# Revit family: 53-40-005-DN32-80
name_source: partatom
category: Pipe Accessories
units: mm (PartAtom-declared; Revit-internal decimal feet)

## family parameters
Always vertical = Yes
Cut with Voids When Loaded = No
Part Type = Valve - Breaks Into
Round Connector Dimension = Use Diameter
Shared = No
Work Plane-Based = No

## types (5) — shared parameters
Body_Wall_thickness = 10 mm  [stored 0.0328084 ft]
Circle_cut = 2 mm  [stored 0.00656168 ft]
DN = 50 mm
DN32_PN10 = 53-032-40-9090
DN40_PN10 = 53-040-40-9090
DN50_PN10 = 53-050-40-9090
DN65_PN10 = 53-065-40-9090
DN80_PN10 = 53-080-40-9090
Description_ = AVK BALL CHECK VALVE, THREADED
Ear_Height = 5 mm  [stored 0.0164042 ft]
Ear_width = 5 mm  [stored 0.0164042 ft]
Hook_Distance = 10 mm  [stored 0.0328084 ft]
RF_Thickness = 3 mm  [stored 0.00984252 ft]
Search_table = 53-40-005-DN32-80
URL product pages = https://www.avkvalves.com

## per-type parameters (varying)
- DN050: Body_Height_1=33 mm  [stored 0.108268 ft]; Body_Height_2=77 mm; Body_Height_3=37 mm  [stored 0.121391 ft]; Body_Ref=71 mm; Body_distance_1=10 mm  [stored 0.0328084 ft]; Body_distance_3=20 mm  [stored 0.0656168 ft]; Bottom_height=5 mm  [stored 0.0164042 ft]; Chamfer=20 mm  [stored 0.0656168 ft]; Chamfer_Ref=46 mm  [stored 0.150919 ft]; Circle_Height=20 mm  [stored 0.0656168 ft]; Circle_Height_2=10 mm  [stored 0.0328084 ft]; Circle_Length=35 mm  [stored 0.114829 ft]; Circle_Radius_2=475 mm; Circle_radius=40 mm  [stored 0.131234 ft]; Cut_Height_Ref=67.33 mm; Cut_ref=35 mm  [stored 0.114829 ft]; DN_ref=70 mm; Distance_1=5 mm  [stored 0.0164042 ft]; Distance_2=51 mm; Distance_3=67 mm; Distance_4=2 mm  [stored 0.00656168 ft]; Ear_Lenght_2=31 mm  [stored 0.101706 ft]; Ear_Length=62 mm; Ear_Reference=73 mm; Ear_Reference_2=3 mm  [stored 0.00984252 ft]; F_OD=82.5 mm; Fillet_Thickness_2=3 mm  [stored 0.00984252 ft]; Flange_Dia=43 mm  [stored 0.141076 ft]; Flange_Thickness=19 mm  [stored 0.062336 ft]; Flange_Thickness_2=5 mm  [stored 0.0164042 ft]; H=101 mm; H3=144 mm; H3_ref=43 mm  [stored 0.141076 ft]; Hook_Distance_2=2 mm  [stored 0.00656168 ft]; Hook_Height=10 mm  [stored 0.0328084 ft]; Hook_Height_2=5 mm  [stored 0.0164042 ft]; Hook_Legnth=5 mm  [stored 0.0164042 ft]; ID=25 mm  [stored 0.082021 ft]; L=180 mm; L2=270 mm; Nominal_Diameter=50 mm; RF=49 mm  [stored 0.160761 ft]; Rib_Distance=10 mm  [stored 0.0328084 ft]; Rib_Distance_2=10 mm  [stored 0.0328084 ft]; Rib_height=20 mm  [stored 0.0656168 ft]
- DN032: Body_Height_1=26 mm; Body_Height_2=55 mm; Body_Height_3=29 mm  [stored 0.0951444 ft]; Body_Ref=51 mm; Body_distance_1=8 mm  [stored 0.0262467 ft]; Body_distance_3=15 mm  [stored 0.0492126 ft]; Bottom_height=3 mm  [stored 0.00984252 ft]; Chamfer=15 mm  [stored 0.0492126 ft]; Chamfer_Ref=35.5 mm  [stored 0.11647 ft]; Circle_Height=12 mm  [stored 0.0393701 ft]; Circle_Height_2=8 mm  [stored 0.0262467 ft]; Circle_Length=25 mm  [stored 0.082021 ft]; Circle_Radius_2=320 mm; Circle_radius=30 mm  [stored 0.0984252 ft]; Cut_Height_Ref=55.33 mm; Cut_ref=26 mm; DN_ref=52 mm; Distance_1=2 mm  [stored 0.00656168 ft]; Distance_2=40 mm  [stored 0.131234 ft]; Distance_3=55 mm; Distance_4=10 mm  [stored 0.0328084 ft]; Ear_Lenght_2=26.75 mm  [stored 0.0877625 ft]; Ear_Length=53.5 mm; Ear_Reference=65 mm; Ear_Reference_2=3 mm  [stored 0.00984252 ft]; F_OD=77.5 mm; Fillet_Thickness_2=3 mm  [stored 0.00984252 ft]; Flange_Dia=31 mm  [stored 0.101706 ft]; Flange_Thickness=19 mm  [stored 0.062336 ft]; Flange_Thickness_2=4 mm  [stored 0.0131234 ft]; H=83 mm; H3=118 mm; H3_ref=35 mm  [stored 0.114829 ft]; Hook_Distance_2=2 mm  [stored 0.00656168 ft]; Hook_Height=10 mm  [stored 0.0328084 ft]; Hook_Height_2=5 mm  [stored 0.0164042 ft]; Hook_Legnth=5 mm  [stored 0.0164042 ft]; ID=16 mm  [stored 0.0524934 ft]; L=140 mm; L2=210 mm; Nominal_Diameter=32 mm  [stored 0.104987 ft]; RF=44 mm  [stored 0.144357 ft]; Rib_Distance=10 mm  [stored 0.0328084 ft]; Rib_Distance_2=10 mm  [stored 0.0328084 ft]; Rib_height=15 mm  [stored 0.0492126 ft]
- DN040: Body_Height_1=30 mm  [stored 0.0984252 ft]; Body_Height_2=55 mm; Body_Height_3=30 mm  [stored 0.0984252 ft]; Body_Ref=51 mm; Body_distance_1=8 mm  [stored 0.0262467 ft]; Body_distance_3=15 mm  [stored 0.0492126 ft]; Bottom_height=3 mm  [stored 0.00984252 ft]; Chamfer=15 mm  [stored 0.0492126 ft]; Chamfer_Ref=35.5 mm  [stored 0.11647 ft]; Circle_Height=15 mm  [stored 0.0492126 ft]; Circle_Height_2=8 mm  [stored 0.0262467 ft]; Circle_Length=27 mm  [stored 0.0885827 ft]; Circle_Radius_2=320 mm; Circle_radius=30 mm  [stored 0.0984252 ft]; Cut_Height_Ref=55.33 mm; Cut_ref=30 mm  [stored 0.0984252 ft]; DN_ref=60 mm; Distance_1=2 mm  [stored 0.00656168 ft]; Distance_2=35 mm  [stored 0.114829 ft]; Distance_3=57 mm; Distance_4=15 mm  [stored 0.0492126 ft]; Ear_Lenght_2=26.75 mm  [stored 0.0877625 ft]; Ear_Length=53.5 mm; Ear_Reference=65 mm; Ear_Reference_2=3 mm  [stored 0.00984252 ft]; F_OD=77.5 mm; Fillet_Thickness_2=3 mm  [stored 0.00984252 ft]; Flange_Dia=31 mm  [stored 0.101706 ft]; Flange_Thickness=19 mm  [stored 0.062336 ft]; Flange_Thickness_2=4 mm  [stored 0.0131234 ft]; H=83 mm; H3=118 mm; H3_ref=35 mm  [stored 0.114829 ft]; Hook_Distance_2=2 mm  [stored 0.00656168 ft]; Hook_Height=10 mm  [stored 0.0328084 ft]; Hook_Height_2=5 mm  [stored 0.0164042 ft]; Hook_Legnth=5 mm  [stored 0.0164042 ft]; ID=20 mm  [stored 0.0656168 ft]; L=140 mm; L2=210 mm; Nominal_Diameter=40 mm  [stored 0.131234 ft]; RF=44 mm  [stored 0.144357 ft]; Rib_Distance=10 mm  [stored 0.0328084 ft]; Rib_Distance_2=10 mm  [stored 0.0328084 ft]; Rib_height=15 mm  [stored 0.0492126 ft]
- DN065: Body_Height_1=36 mm  [stored 0.11811 ft]; Body_Height_2=120 mm; Body_Height_3=48 mm  [stored 0.15748 ft]; Body_Ref=103.5 mm; Body_distance_1=17 mm  [stored 0.0557743 ft]; Body_distance_3=35 mm  [stored 0.114829 ft]; Bottom_height=15 mm  [stored 0.0492126 ft]; Chamfer=35 mm  [stored 0.114829 ft]; Chamfer_Ref=60.5 mm; Circle_Height=23 mm  [stored 0.0754593 ft]; Circle_Height_2=15 mm  [stored 0.0492126 ft]; Circle_Length=45 mm  [stored 0.147638 ft]; Circle_Radius_2=475 mm; Circle_radius=62 mm; Cut_Height_Ref=93.33 mm; Cut_ref=42.5 mm  [stored 0.139436 ft]; DN_ref=85 mm; Distance_1=5 mm  [stored 0.0164042 ft]; Distance_2=80 mm; Distance_3=90 mm; Distance_4=2 mm  [stored 0.00656168 ft]; Ear_Lenght_2=46.5 mm  [stored 0.152559 ft]; Ear_Length=93 mm; Ear_Reference=50 mm; Ear_Reference_2=15 mm  [stored 0.0492126 ft]; F_OD=92.5 mm; Fillet_Thickness_2=3 mm  [stored 0.00984252 ft]; Flange_Dia=66 mm; Flange_Thickness=19 mm  [stored 0.062336 ft]; Flange_Thickness_2=11 mm  [stored 0.0360892 ft]; H=140 mm; H3=196 mm; H3_ref=56 mm; Hook_Distance_2=10 mm  [stored 0.0328084 ft]; Hook_Height=15 mm  [stored 0.0492126 ft]; Hook_Height_2=10 mm  [stored 0.0328084 ft]; Hook_Legnth=5 mm  [stored 0.0164042 ft]; ID=32.5 mm  [stored 0.106627 ft]; L=245 mm; L2=367.5 mm; Nominal_Diameter=65 mm; RF=59 mm; Rib_Distance=30 mm  [stored 0.0984252 ft]; Rib_Distance_2=30 mm  [stored 0.0984252 ft]; Rib_height=30 mm  [stored 0.0984252 ft]
- DN080: Body_Height_1=40 mm  [stored 0.131234 ft]; Body_Height_2=105 mm; Body_Height_3=57 mm; Body_Ref=112 mm; Body_distance_1=19 mm  [stored 0.062336 ft]; Body_distance_3=30 mm  [stored 0.0984252 ft]; Bottom_height=15 mm  [stored 0.0492126 ft]; Chamfer=22 mm  [stored 0.0721785 ft]; Chamfer_Ref=63 mm; Circle_Height=30 mm  [stored 0.0984252 ft]; Circle_Height_2=30 mm  [stored 0.0984252 ft]; Circle_Length=50 mm; Circle_Radius_2=1779 mm; Circle_radius=63.5 mm; Cut_Height_Ref=93.33 mm; Cut_ref=50 mm; DN_ref=100 mm; Distance_1=2 mm  [stored 0.00656168 ft]; Distance_2=80 mm; Distance_3=89 mm; Distance_4=5 mm  [stored 0.0164042 ft]; Ear_Lenght_2=46.5 mm  [stored 0.152559 ft]; Ear_Length=93 mm; Ear_Reference=103 mm; Ear_Reference_2=9 mm  [stored 0.0295276 ft]; F_OD=100 mm; Fillet_Thickness_2=5 mm  [stored 0.0164042 ft]; Flange_Dia=63 mm; Flange_Thickness=18 mm  [stored 0.0590551 ft]; Flange_Thickness_2=10 mm  [stored 0.0328084 ft]; H=140 mm; H3=198 mm; H3_ref=58 mm; Hook_Distance_2=10 mm  [stored 0.0328084 ft]; Hook_Height=20 mm  [stored 0.0656168 ft]; Hook_Height_2=15 mm  [stored 0.0492126 ft]; Hook_Legnth=10 mm  [stored 0.0328084 ft]; ID=40 mm  [stored 0.131234 ft]; L=260 mm; L2=390 mm; Nominal_Diameter=80 mm; RF=80 mm; Rib_Distance=40 mm  [stored 0.131234 ft]; Rib_Distance_2=40 mm  [stored 0.131234 ft]; Rib_height=35 mm  [stored 0.114829 ft]

note: [stored X ft] marks values corroborated as IEEE doubles in the binary element streams (Revit-internal decimal feet)

## geometry (parser evidence)
native form markers: Sweep x11
no freeform markers — native parametric forms only
